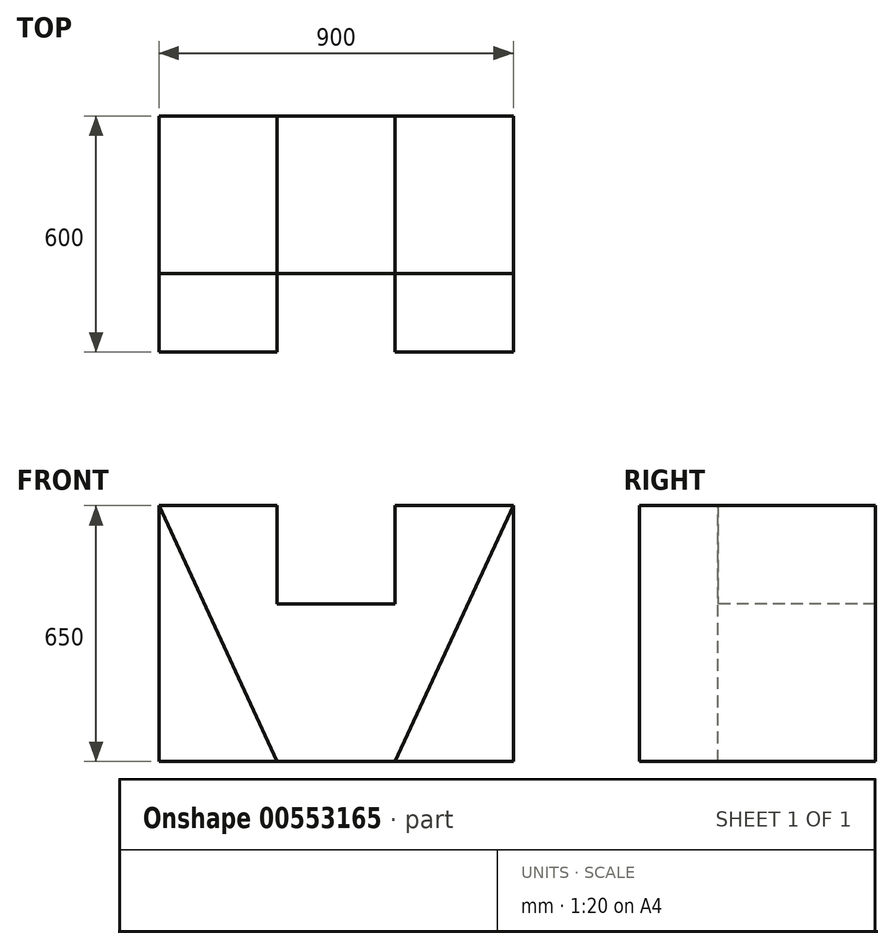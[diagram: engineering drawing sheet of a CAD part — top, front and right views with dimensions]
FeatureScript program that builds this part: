
annotation { "Feature Type Name" : "Feature", "Feature Type Description" : "" }
export const myFeature = defineFeature(function(context is Context, id is Id, definition is map)
    precondition{}
    {
        {
            var Q0;
            Q0=qCreatedBy(makeId("Front.planeOp"),FACE);
            var sketch = newSketch(context, id + "F0", { "sketchPlane" : qUnion([Q0])});
            skLineSegment(sketch, "E0.bottom", {"start": v(450, 325) * mm, "end": v(-450, 325) * mm});
            skLineSegment(sketch, "E0.top", {"start": v(450, -325) * mm, "end": v(-450, -325) * mm});
            skLineSegment(sketch, "E0.left", {"start": v(450, 325) * mm, "end": v(450, -325) * mm});
            skLineSegment(sketch, "E0.right", {"start": v(-450, 325) * mm, "end": v(-450, -325) * mm});
            skPoint(sketch, "E0.middle", {"position": v(0, 0) * mm});
            skSolve(sketch);
        }
        {
            var Q0;
            Q0=makeQuery(id+"F0.imprint","IMPRINT",FACE,{"disambiguationData":[TD([[makeQuery(id+"F0.imprint","IMPRINT",EDGE,{"derivedFrom":sQuery(id+"F0.wireOp",EDGE,"E0.bottom")}),1.0]])]});
            extrude(context, id + "F1", {"entities" : qUnion([Q0]), "depth" : 400 * mm, "offsetDistance" : 25.4 * mm});
        }
        {
            var Q0;
            Q0=makeQuery(id+"F1.opExtrude","CAP_FACE",FACE,{"disambiguationData":[OSD([sQuery(id+"F0.wireOp",EDGE,"E0.bottom"),sQuery(id+"F0.wireOp",EDGE,"E0.top"),sQuery(id+"F0.wireOp",EDGE,"E0.left"),sQuery(id+"F0.wireOp",EDGE,"E0.right")])],"isStart":false});
            var sketch = newSketch(context, id + "F2", { "sketchPlane" : qUnion([Q0])});
            skLineSegment(sketch, "E1.top", {"start": v(150, 75) * mm, "end": v(-150, 75) * mm});
            skLineSegment(sketch, "E1.left", {"start": v(150, 325) * mm, "end": v(150, 75) * mm});
            skLineSegment(sketch, "E1.right", {"start": v(-150, 325) * mm, "end": v(-150, 75) * mm});
            skPoint(sketch, "E1.middle", {"position": v(0, 325) * mm});
            skPoint(sketch, "E2.orphan", {"position": v(150, 575) * mm});
            skPoint(sketch, "E3.orphan", {"position": v(-150, 575) * mm});
            skSolve(sketch);
        }
        {
            var Q0;
            Q0 = qSketchRegion(id + "F2", true);
            var Q1;
            Q1=makeQuery(id+"F2.imprint","IMPRINT",FACE,{"disambiguationData":[TD([[makeQuery(id+"F2.imprint","IMPRINT",EDGE,{"derivedFrom":sQuery(id+"F2.wireOp",EDGE,"E1.top")}),-1.0]])]});
            extrude(context, id + "F3", {"entities" : qUnion([Q0, Q1]), "operationType" : NewBodyOperationType.REMOVE, "endBound" : BoundingType.THROUGH_ALL, "oppositeDirection" : true, "depth" : 25.4 * mm, "offsetDistance" : 25.4 * mm});
        }
        {
            var Q0;
            Q0=makeQuery(id+"F1.opExtrude","CAP_FACE",FACE,{"disambiguationData":[OSD([sQuery(id+"F0.wireOp",EDGE,"E0.bottom"),sQuery(id+"F0.wireOp",EDGE,"E0.top"),sQuery(id+"F0.wireOp",EDGE,"E0.left"),sQuery(id+"F0.wireOp",EDGE,"E0.right")])],"isStart":false});
            var sketch = newSketch(context, id + "F4", { "sketchPlane" : qUnion([Q0])});
            skLineSegment(sketch, "E4", {"start": v(-450, 325) * mm, "end": v(-150, -325) * mm});
            skLineSegment(sketch, "E5", {"start": v(-150, -325) * mm, "end": v(-450, -325) * mm});
            skLineSegment(sketch, "E6", {"start": v(-450, -325) * mm, "end": v(-450, 325) * mm});
            skLineSegment(sketch, "E7", {"start": v(-450, 325) * mm, "end": v(-450, -325) * mm});
            skLineSegment(sketch, "E8", {"start": v(450, 325) * mm, "end": v(450, -325) * mm});
            skLineSegment(sketch, "E9", {"start": v(450, -325) * mm, "end": v(150, -325) * mm});
            skLineSegment(sketch, "E10", {"start": v(150, -325) * mm, "end": v(450, 325) * mm});
            skSolve(sketch);
        }
        {
            var Q0;
            Q0 = qSketchRegion(id + "F4", true);
            extrude(context, id + "F5", {"entities" : qUnion([Q0]), "operationType" : NewBodyOperationType.ADD, "depth" : 200 * mm, "offsetDistance" : 25.4 * mm});
        }
    });
